# Revit family: Toilet-Elongated_Traditional_Dartmouth_ADA_CST754SF_TOTO
name_source: partatom
category: Plumbing Fixtures
revit_build: Autodesk Revit Architecture 2013 (Build: 20130531_2115(x64)
units: mm (PartAtom-declared; Revit-internal decimal feet)

## types (1)
- CST754SF
    04 CSI = 22 42 13
    95 CSI = 15410-800
    ADA Compliant = Yes
    Assembly Code = D2010110
    Bowl Material = Vitreous China
    CAD Drawing URL = http://assets.totousa.com
    CW Connection = Yes
    CWFU = 0
    Certifications = IAPMO (cUPC), State of Massachusetts, City of Los Angeles, and others
    Code Compliance = UPC, IPC, NSPC, NPC Canada, and others
    Cold Water Connection NPT Radius = 0' - 0 1/4"
    Color Availability = #01 Cotton, #03 Bone, #11 Colonial White, #12 Sedona Beige, #51 Ebony
    Default Elevation = 0' - 0"
    Description = Classic Design Two-Piece Toilet
    Finish = Vitreous China - TOTO - 01 Cotton
    Flush System = G-Max
    Gallons Per Flush = 1.6 gal
    HW Connection = No
    HWFU = 0
    Height = 2' - 8 1/2"
    Industry Standards = Meets and exceeds ASME A112.19.2/CSA B45.1
    Length = 2' - 5 1/2"
    Manufacturer = TOTO USA, Inc.
    Manufacturer Fax = (770) 282-0002
    Model = CST754SF
    Mount Type = Floor-Mounted
    Rough in Availability = 12"
    Rough in Distance = 1' - 0"
    Sanitary Horizontal Offset from Wall = 0' - 11 13/32"
    SanoGloss Available = No
    Series = Dartmouth
    Shipping Weight = 95.50 lb
    Spec Sheet URL = http://assets.totousa.com
    Style = Traditional
    Subcategory = Toilets
    Supply Horizontal Offset from Center = 0' - 6"
    Supply Vertical Offset from Floor = 0' - 8"
    Toto BIM Number = BM-00093
    URL = http://www.totousa.com
    Vent Connection = Yes
    WFU = 0
    Warranty = One Year Limited Warranty
    Warranty URL = http://www.totousa.com
    Waste Connection = Yes
    WaterSense = No
    Width = 1' - 8 5/8"

## geometry (parser evidence)
native form markers: Blend x16, Sweep x2
no freeform markers — native parametric forms only
